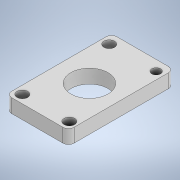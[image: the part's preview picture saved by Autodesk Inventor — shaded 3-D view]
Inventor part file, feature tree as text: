
AUTODESK INVENTOR PART (.ipt)
format: ipt  version: 2020 (Build 240168000, 168)  size: 128,000 bytes
history: native  units: mm
features: fillet x4, extrude x1, sketch x1
ambient origin geometry x8: Origin, YZ Plane, XZ Plane, XY Plane, X Axis, Y Axis, Z Axis, Center Point
bodies: Body1 (feature_tree)
feature tree (6):
  extrude  "Extrusion2"  Depth=2.0mm
  fillet  "Fillet1"  Radius=2.0mm
  fillet  "Fillet2"  Radius=2.0mm
  fillet  "Fillet3"  Radius=2.0mm
  fillet  "Fillet4"  Radius=0.5mm
  sketch  "Sketch2"  dims[d2=5.0mm d3=0.0mm d4=2.0mm d5=2.0mm d6=2.0mm d7=2.0mm d0=0.5mm d1=0.872665mm]
